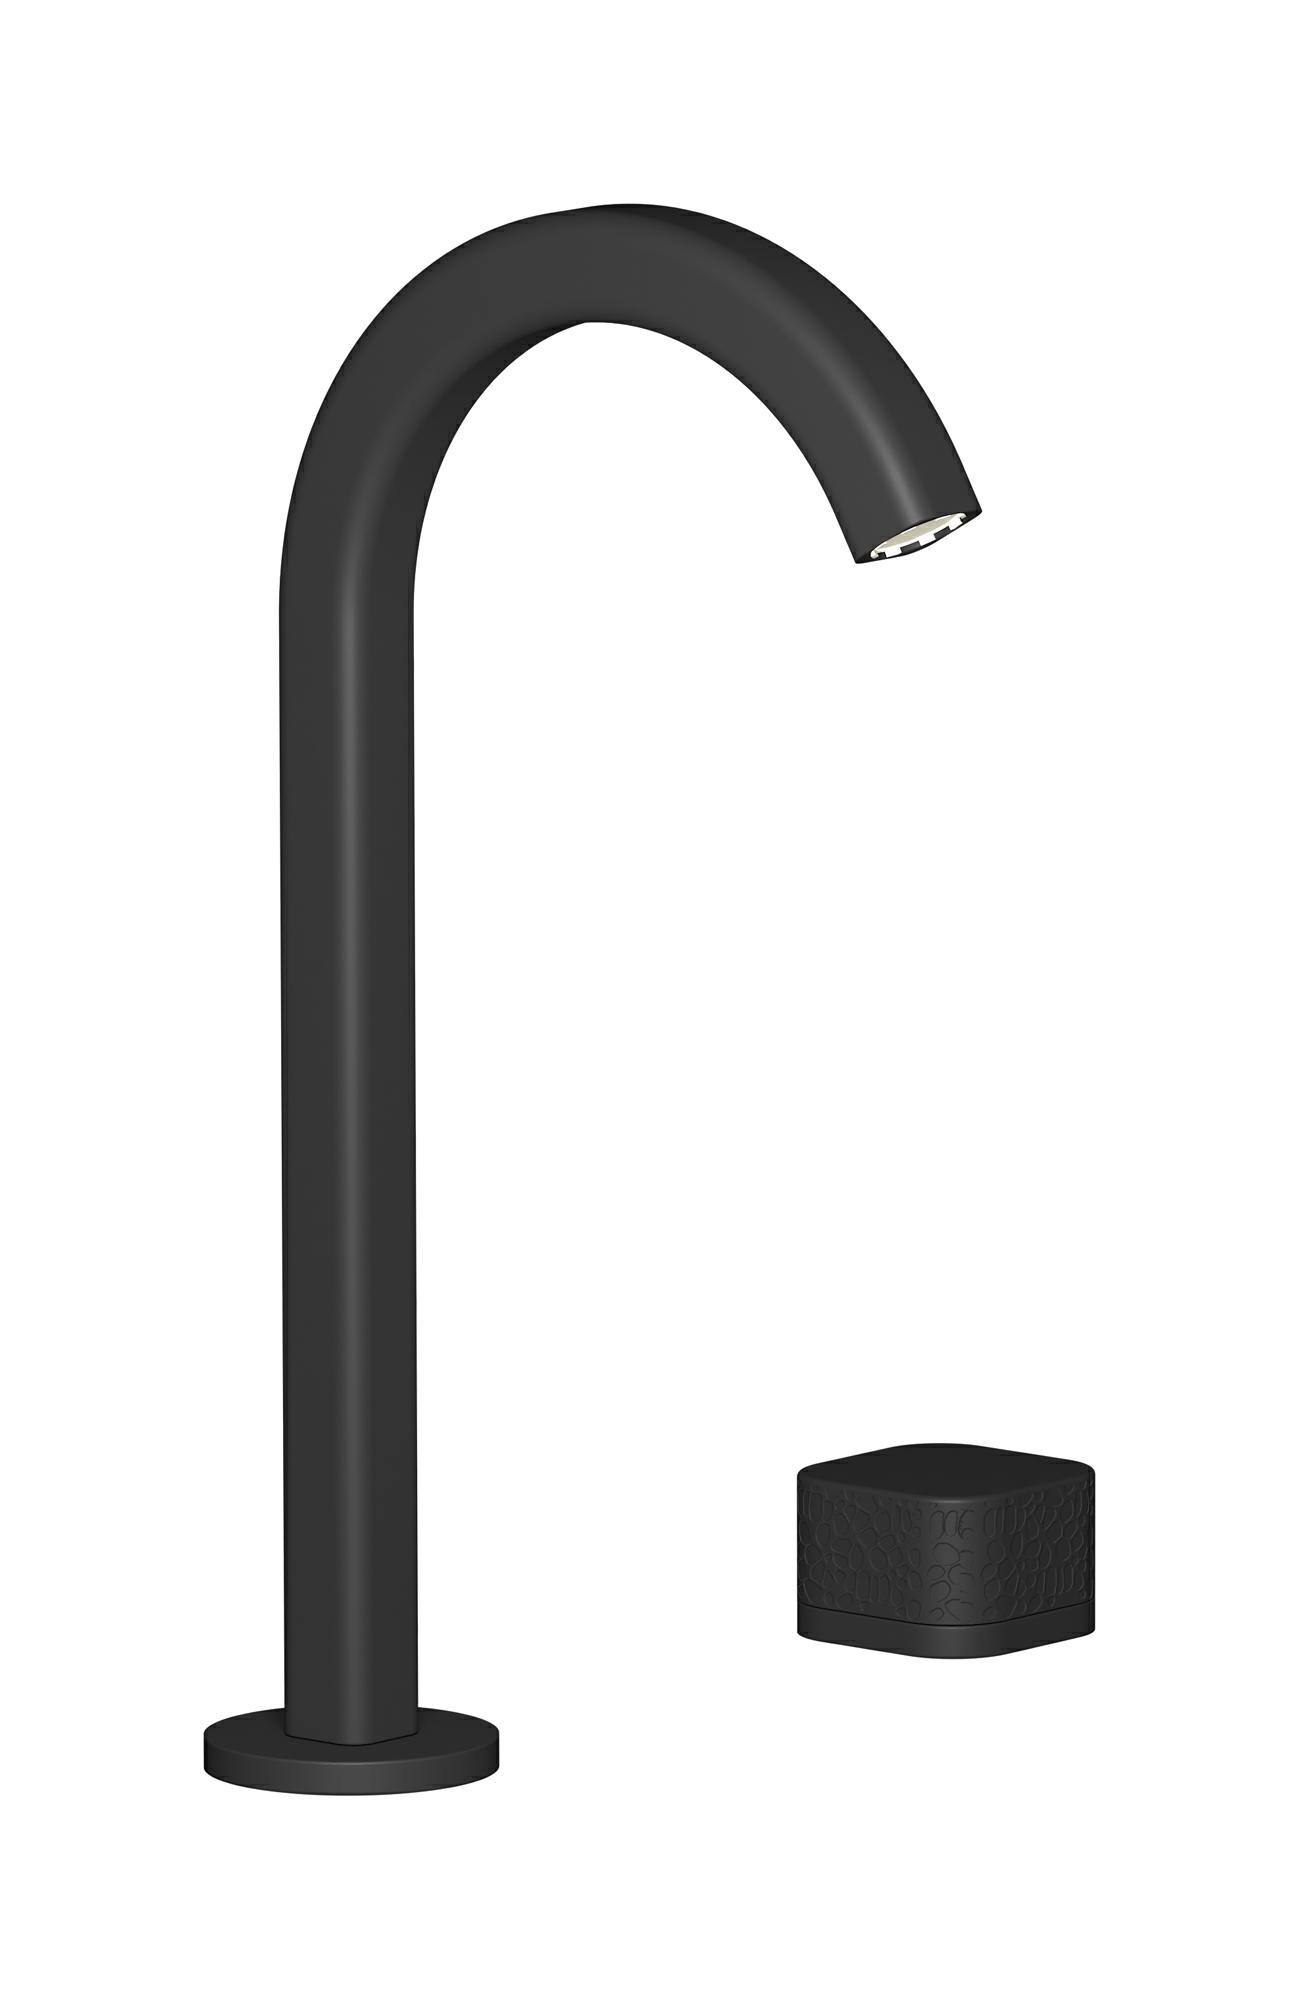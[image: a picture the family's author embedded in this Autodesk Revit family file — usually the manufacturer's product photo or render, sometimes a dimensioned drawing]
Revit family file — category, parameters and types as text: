
# Revit family: EO394_2
name_source: partatom
category: Apparecchi idraulici
units: mm (PartAtom-declared; Revit-internal decimal feet)

## family parameters
Basato su piano di lavoro = No
Condiviso = No
Mantieni orientamento annotazione = No
Numero OmniClass = 23.45.55.17
Punto di calcolo locali = No
Quota connettore circolare = Usa diametro
Sempre verticale = Sì
Taglio con vuoti quando caricato = No
Tipo di parte = Normale
Titolo OmniClass = Mixing Faucets

## types (12) — shared parameters
Cold water inlet = 10 mm  [stored 0.0328084 ft]
Commenti sul tipo = Washbasin
Connessione CW = No
Connessione HW = No
Connessione di scarico = No
Connessione di ventilazione = No
Descrizione = Washbasin two hole mixer
Hot water inlet = 10 mm  [stored 0.0328084 ft]
Produttore = IB Rubinetterie S.p.A.
URL = https://www.weareib.it
zero-valued in all types: Prospetto di default

## per-type parameters (varying)
| type | Finishes surface | Immagine tipo | Modello |
| Chrome | IB_Chrome | EO394CC_2.jpg | EO394CC_2 |
| Brushed nickel | IB_Brushed nickel | EO394SS_2.jpg | EO394SS_2 |
| Matt black | IB_matt black | EO394NP_2.jpg | EO394NP_2 |
| Natural brass | IB_Brass | EO394ON_2.jpg | EO394ON_2 |
| Black chrome | IB_Black chrome | EO394CF_2.jpg | EO394CF_2 |
| Brushed black chrome | IB_Brushed black chrome | EO394CS_2.jpg | EO394CS_2 |
| Pale gold | IB_Pale gold | EO394II_2.jpg | EO394II_2 |
| Brushed pale gold | IB_brushed pale gold | EO394IS_2.jpg | EO394IS_2 |
| Rose gold | IB_Rose gold | EO394RS_2.jpg | EO394RS_2 |
| Brushed rose gold | IB_Brushed rose gold | EO394SR_2.jpg | EO394SR_2 |
| Gold | IB_gold | EO394OO_2.jpg | EO394OO_2 |
| Brushed gold | IB_brushed gold | EO394OS_2.jpg | EO394OS_2 |

note: [stored X ft] marks values corroborated as IEEE doubles in the binary element streams (Revit-internal decimal feet)
